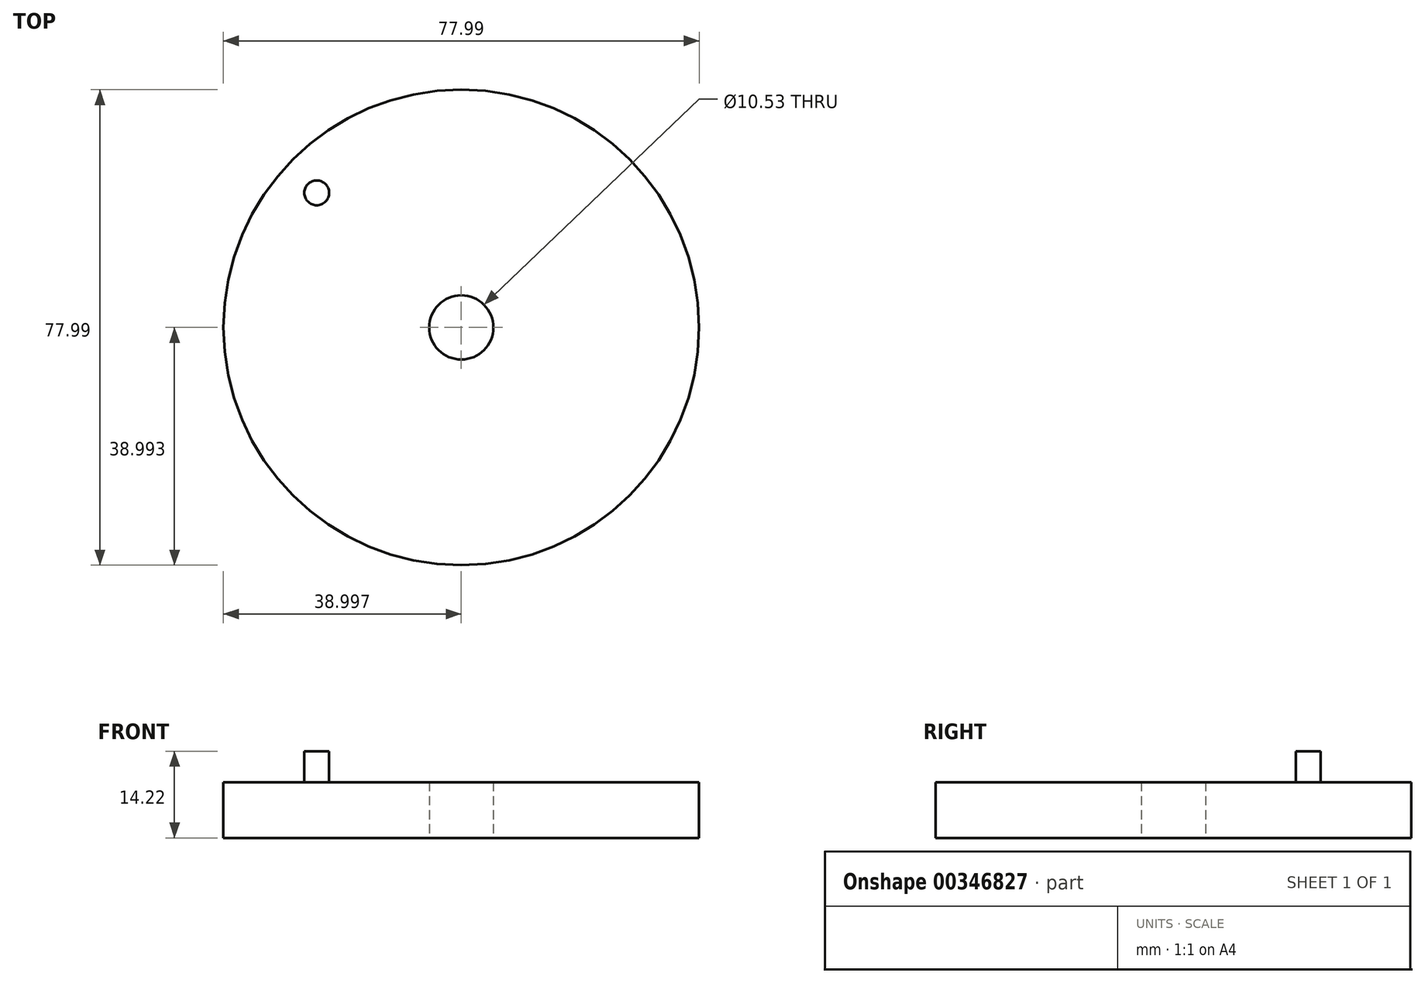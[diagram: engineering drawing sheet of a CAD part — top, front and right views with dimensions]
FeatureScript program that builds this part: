
annotation { "Feature Type Name" : "Feature", "Feature Type Description" : "" }
export const myFeature = defineFeature(function(context is Context, id is Id, definition is map)
    precondition{}
    {
        {
            var Q0;
            Q0=qCreatedBy(makeId("Top.planeOp"),FACE);
            var sketch = newSketch(context, id + "F0", { "sketchPlane" : qUnion([Q0])});
            skCircle(sketch, "E0", {"center": v(18.22, -16.97) * mm, "radius": 5.26 * mm});
            skCircle(sketch, "E1", {"center": v(-5.48, 5.1) * mm, "radius": 2.03 * mm});
            skCircle(sketch, "E2", {"center": v(18.22, -16.97) * mm, "radius": 39 * mm});
            skLineSegment(sketch, "E3", {"start": v(18.22, -16.97) * mm, "end": v(-5.48, 5.1) * mm});
            skSolve(sketch);
        }
        {
            var Q0;
            Q0=makeQuery(id+"F0.imprint","IMPRINT",FACE,{"disambiguationData":[TD([[makeQuery(id+"F0.imprint","IMPRINT",EDGE,{"derivedFrom":sQuery(id+"F0.wireOp",EDGE,"E0")}),-1.0]])]});
            var Q1;
            Q1=makeQuery(id+"F0.imprint","IMPRINT",FACE,{"disambiguationData":[TD([[makeQuery(id+"F0.imprint","IMPRINT",EDGE,{"derivedFrom":sQuery(id+"F0.wireOp",EDGE,"E1")}),1.0]])]});
            extrude(context, id + "F1", {"entities" : qUnion([Q0, Q1]), "depth" : 9.14 * mm});
        }
        {
            var Q0;
            Q0=makeQuery(id+"F0.imprint","IMPRINT",FACE,{"disambiguationData":[TD([[makeQuery(id+"F0.imprint","IMPRINT",EDGE,{"derivedFrom":sQuery(id+"F0.wireOp",EDGE,"E1")}),1.0]])]});
            extrude(context, id + "F2", {"entities" : qUnion([Q0]), "operationType" : NewBodyOperationType.ADD, "depth" : 14.22 * mm});
        }
    });
